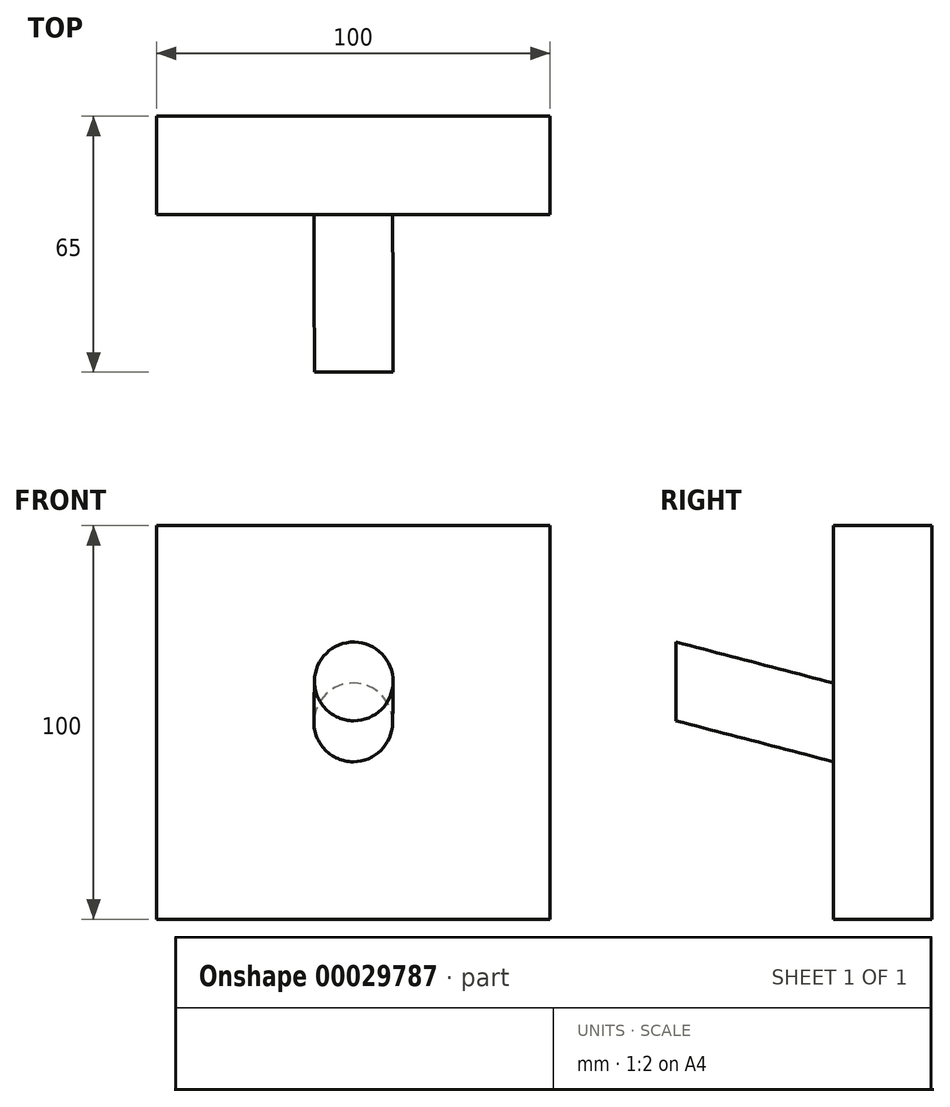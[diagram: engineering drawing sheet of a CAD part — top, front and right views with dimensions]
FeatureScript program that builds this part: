
annotation { "Feature Type Name" : "Feature", "Feature Type Description" : "" }
export const myFeature = defineFeature(function(context is Context, id is Id, definition is map)
    precondition{}
    {
        {
            var Q0;
            Q0=qCreatedBy(makeId("Front.planeOp"),FACE);
            var sketch = newSketch(context, id + "F0", { "sketchPlane" : qUnion([Q0])});
            skLineSegment(sketch, "E0.bottom", {"start": v(0, 0) * mm, "end": v(100, 0) * mm});
            skLineSegment(sketch, "E0.top", {"start": v(0, 100) * mm, "end": v(100, 100) * mm});
            skLineSegment(sketch, "E0.left", {"start": v(0, 0) * mm, "end": v(0, 100) * mm});
            skLineSegment(sketch, "E0.right", {"start": v(100, 0) * mm, "end": v(100, 100) * mm});
            skSolve(sketch);
        }
        {
            var Q0;
            Q0=qSketchRegion(id+"F0",true);
            extrude(context, id + "F1", {"entities" : qUnion([Q0]), "depth" : 25 * mm});
        }
        {
            var Q0;
            Q0=makeQuery(id+"F1.opExtrude","CAP_FACE",FACE,{"disambiguationData":[OSD([sQuery(id+"F0.wireOp",EDGE,"E0.bottom"),sQuery(id+"F0.wireOp",EDGE,"E0.top"),sQuery(id+"F0.wireOp",EDGE,"E0.left"),sQuery(id+"F0.wireOp",EDGE,"E0.right")])],"isStart":false});
            var sketch = newSketch(context, id + "F2", { "sketchPlane" : qUnion([Q0])});
            skCircle(sketch, "E1", {"center": v(50, 50) * mm, "radius": 10 * mm});
            skSolve(sketch);
        }
        {
            var Q0;
            Q0=qCreatedBy(makeId("Front.planeOp"),FACE);
            cPlane(context, id + "F3", {"entities" : qUnion([Q0]), "cplaneType" : CPlaneType.OFFSET, "offset" : 65 * mm, "width" : 150 * mm, "height" : 150 * mm});
        }
        {
            var Q0;
            Q0=qCreatedBy(id+"F3.planeOp",FACE);
            var sketch = newSketch(context, id + "F4", { "sketchPlane" : qUnion([Q0])});
            skLineSegment(sketch, "E2", {"start": v(50.14, 50.3) * mm, "end": v(84.39, 50.3) * mm});
            skLineSegment(sketch, "E3.0", {"start": v(50.14, 60.42) * mm, "end": v(84.39, 60.42) * mm});
            skCircle(sketch, "E4", {"center": v(50.14, 60.42) * mm, "radius": 10 * mm});
            skSolve(sketch);
        }
        {
            var Q1;
            Q1=makeQuery(id+"F2.imprint","IMPRINT",FACE,{"disambiguationData":[TD([[makeQuery(id+"F2.imprint","IMPRINT",EDGE,{"derivedFrom":sQuery(id+"F2.wireOp",EDGE,"E1")}),1.0]])]});
            var Q2;
            Q2=makeQuery(id+"F4.imprint","IMPRINT",FACE,{"disambiguationData":[TD([[makeQuery(id+"F4.imprint","IMPRINT",EDGE,{"derivedFrom":sQuery(id+"F4.wireOp",EDGE,"E4")}),1.0]])]});
            loft(context, id + "F5", {"operationType" : NewBodyOperationType.ADD, "sheetProfilesArray" : [{ "sheetProfileEntities" : qUnion([Q1]) }, { "sheetProfileEntities" : qUnion([Q2]) }]});
        }
    });
